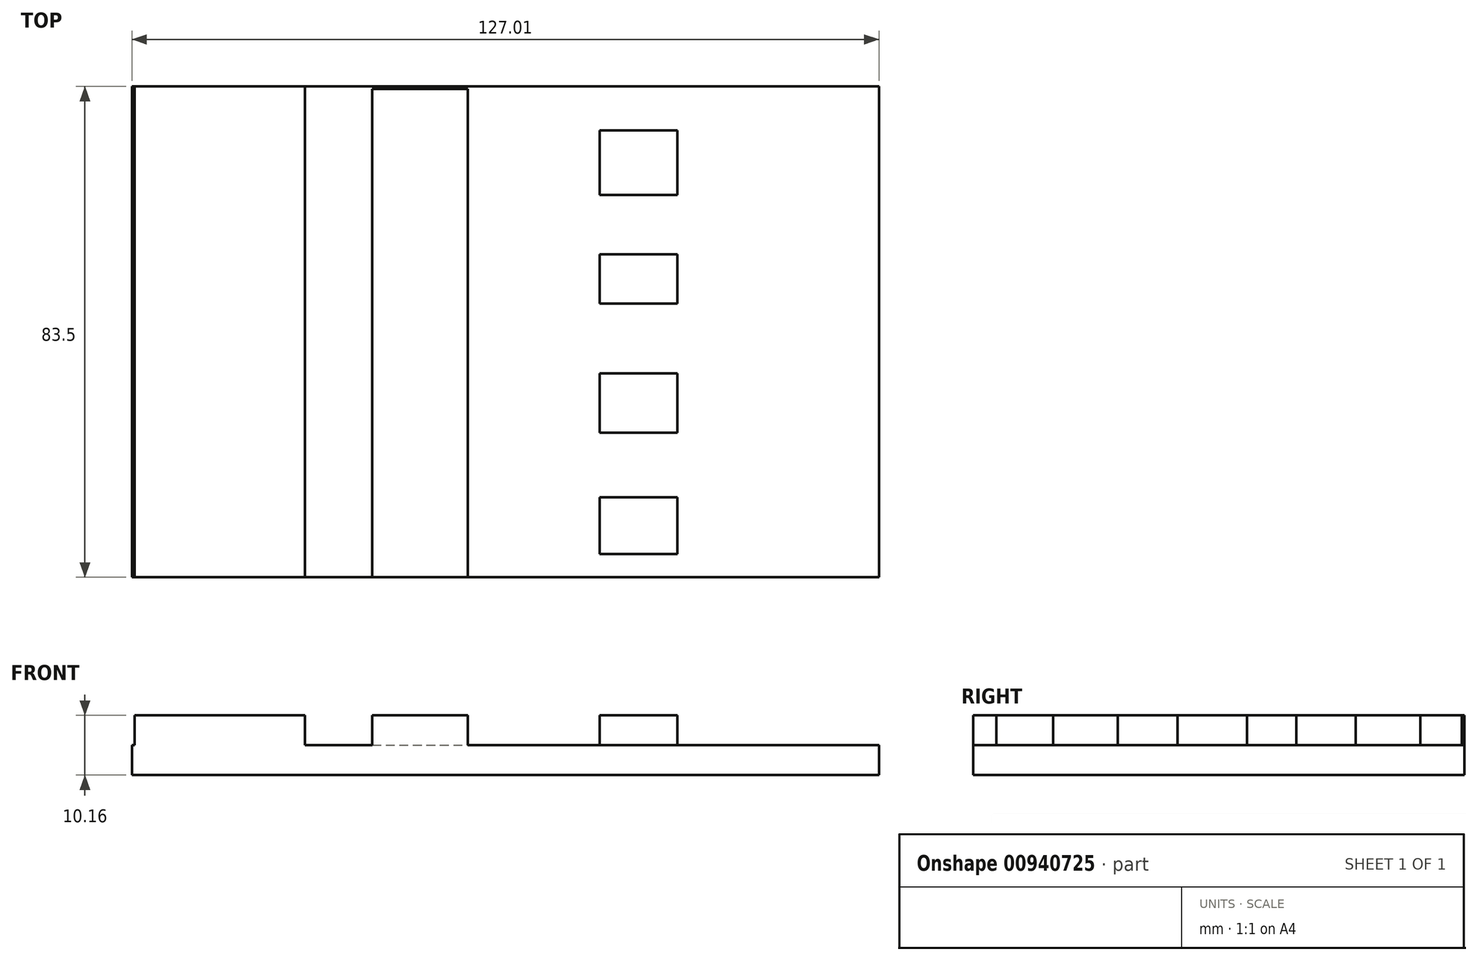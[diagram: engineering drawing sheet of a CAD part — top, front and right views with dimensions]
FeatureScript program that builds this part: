
annotation { "Feature Type Name" : "Feature", "Feature Type Description" : "" }
export const myFeature = defineFeature(function(context is Context, id is Id, definition is map)
    precondition{}
    {
        {
            var Q0;
            Q0=qCreatedBy(makeId("Top.planeOp"),FACE);
            var sketch = newSketch(context, id + "F0", { "sketchPlane" : qUnion([Q0])});
            skLineSegment(sketch, "E0.bottom", {"start": v(-57.13, 40.65) * mm, "end": v(69.88, 40.65) * mm});
            skLineSegment(sketch, "E0.top", {"start": v(-57.13, -42.85) * mm, "end": v(69.88, -42.85) * mm});
            skLineSegment(sketch, "E0.left", {"start": v(-57.13, 40.65) * mm, "end": v(-57.13, -42.85) * mm});
            skLineSegment(sketch, "E0.right", {"start": v(69.88, 40.65) * mm, "end": v(69.88, -42.85) * mm});
            skSolve(sketch);
        }
        {
            var Q0;
            Q0=makeQuery(id+"F0.imprint","IMPRINT",FACE,{"disambiguationData":[TD([[makeQuery(id+"F0.imprint","IMPRINT",EDGE,{"derivedFrom":sQuery(id+"F0.wireOp",EDGE,"E0.bottom")}),-1.0]])]});
            var sketch = newSketch(context, id + "F1", { "sketchPlane" : qUnion([Q0])});
            skLineSegment(sketch, "E1.bottom", {"start": v(-27.69, 40.65) * mm, "end": v(-56.7, 40.65) * mm});
            skLineSegment(sketch, "E1.top", {"start": v(-27.69, -42.85) * mm, "end": v(-56.7, -42.85) * mm});
            skLineSegment(sketch, "E1.left", {"start": v(-27.69, 40.65) * mm, "end": v(-27.69, -42.85) * mm});
            skLineSegment(sketch, "E1.right", {"start": v(-56.7, 40.65) * mm, "end": v(-56.7, -42.85) * mm});
            skLineSegment(sketch, "E2.bottom", {"start": v(-16.26, 40.21) * mm, "end": v(0, 40.21) * mm});
            skLineSegment(sketch, "E2.top", {"start": v(-16.26, -42.85) * mm, "end": v(0, -42.85) * mm});
            skLineSegment(sketch, "E2.left", {"start": v(-16.26, 40.21) * mm, "end": v(-16.26, -42.85) * mm});
            skLineSegment(sketch, "E2.right", {"start": v(0, 40.21) * mm, "end": v(0, -42.85) * mm});
            skLineSegment(sketch, "E3", {"start": v(22.41, 33.18) * mm, "end": v(22.41, 22.2) * mm});
            skLineSegment(sketch, "E4", {"start": v(35.6, 33.18) * mm, "end": v(35.6, 22.2) * mm});
            skLineSegment(sketch, "E5.bottom", {"start": v(22.41, 33.18) * mm, "end": v(35.6, 33.18) * mm});
            skLineSegment(sketch, "E5.top", {"start": v(22.41, 22.2) * mm, "end": v(35.6, 22.2) * mm});
            skLineSegment(sketch, "E6.bottom", {"start": v(22.41, 12.09) * mm, "end": v(35.6, 12.09) * mm});
            skLineSegment(sketch, "E6.top", {"start": v(22.41, 3.74) * mm, "end": v(35.6, 3.74) * mm});
            skLineSegment(sketch, "E6.left", {"start": v(22.41, 12.09) * mm, "end": v(22.41, 3.74) * mm});
            skLineSegment(sketch, "E6.right", {"start": v(35.6, 12.09) * mm, "end": v(35.6, 3.74) * mm});
            skLineSegment(sketch, "E7.bottom", {"start": v(22.41, -8.13) * mm, "end": v(35.6, -8.13) * mm});
            skLineSegment(sketch, "E7.top", {"start": v(22.41, -18.24) * mm, "end": v(35.6, -18.24) * mm});
            skLineSegment(sketch, "E7.left", {"start": v(22.41, -8.13) * mm, "end": v(22.41, -18.24) * mm});
            skLineSegment(sketch, "E7.right", {"start": v(35.6, -8.13) * mm, "end": v(35.6, -18.24) * mm});
            skLineSegment(sketch, "E8.bottom", {"start": v(22.41, -29.23) * mm, "end": v(35.6, -29.23) * mm});
            skLineSegment(sketch, "E8.top", {"start": v(22.41, -38.9) * mm, "end": v(35.6, -38.9) * mm});
            skLineSegment(sketch, "E8.left", {"start": v(22.41, -29.23) * mm, "end": v(22.41, -38.9) * mm});
            skLineSegment(sketch, "E8.right", {"start": v(35.6, -29.23) * mm, "end": v(35.6, -38.9) * mm});
            skPoint(sketch, "E9.orphan", {"position": v(22.41, -43.73) * mm});
            skPoint(sketch, "E10.orphan", {"position": v(35.6, -43.73) * mm});
            skSolve(sketch);
        }
        {
            var Q0;
            Q0 = qSketchRegion(id + "F0", true);
            extrude(context, id + "F2", {"entities" : qUnion([Q0]), "oppositeDirection" : true, "depth" : 5.08 * mm, "offsetDistance" : 25.4 * mm});
        }
        {
            var Q0;
            Q0=makeQuery(id+"F1.imprint","IMPRINT",FACE,{"disambiguationData":[TD([[makeQuery(id+"F1.imprint","IMPRINT",EDGE,{"derivedFrom":sQuery(id+"F1.wireOp",EDGE,"E1.bottom")}),-1.0]])]});
            var Q1;
            Q1=makeQuery(id+"F1.imprint","IMPRINT",FACE,{"disambiguationData":[TD([[makeQuery(id+"F1.imprint","IMPRINT",EDGE,{"derivedFrom":sQuery(id+"F1.wireOp",EDGE,"E2.bottom")}),-1.0]])]});
            var Q2;
            Q2=makeQuery(id+"F1.imprint","IMPRINT",FACE,{"disambiguationData":[TD([[makeQuery(id+"F1.imprint","IMPRINT",EDGE,{"derivedFrom":sQuery(id+"F1.wireOp",EDGE,"E5.bottom")}),-1.0]])]});
            var Q3;
            Q3=makeQuery(id+"F1.imprint","IMPRINT",FACE,{"disambiguationData":[TD([[makeQuery(id+"F1.imprint","IMPRINT",EDGE,{"derivedFrom":sQuery(id+"F1.wireOp",EDGE,"E6.bottom")}),-1.0]])]});
            var Q4;
            Q4=makeQuery(id+"F1.imprint","IMPRINT",FACE,{"disambiguationData":[TD([[makeQuery(id+"F1.imprint","IMPRINT",EDGE,{"derivedFrom":sQuery(id+"F1.wireOp",EDGE,"E7.bottom")}),-1.0]])]});
            var Q5;
            Q5=makeQuery(id+"F1.imprint","IMPRINT",FACE,{"disambiguationData":[TD([[makeQuery(id+"F1.imprint","IMPRINT",EDGE,{"derivedFrom":sQuery(id+"F1.wireOp",EDGE,"E8.bottom")}),-1.0]])]});
            extrude(context, id + "F3", {"entities" : qUnion([Q0, Q1, Q2, Q3, Q4, Q5]), "operationType" : NewBodyOperationType.ADD, "depth" : 5.08 * mm, "offsetDistance" : 25.4 * mm});
        }
    });
